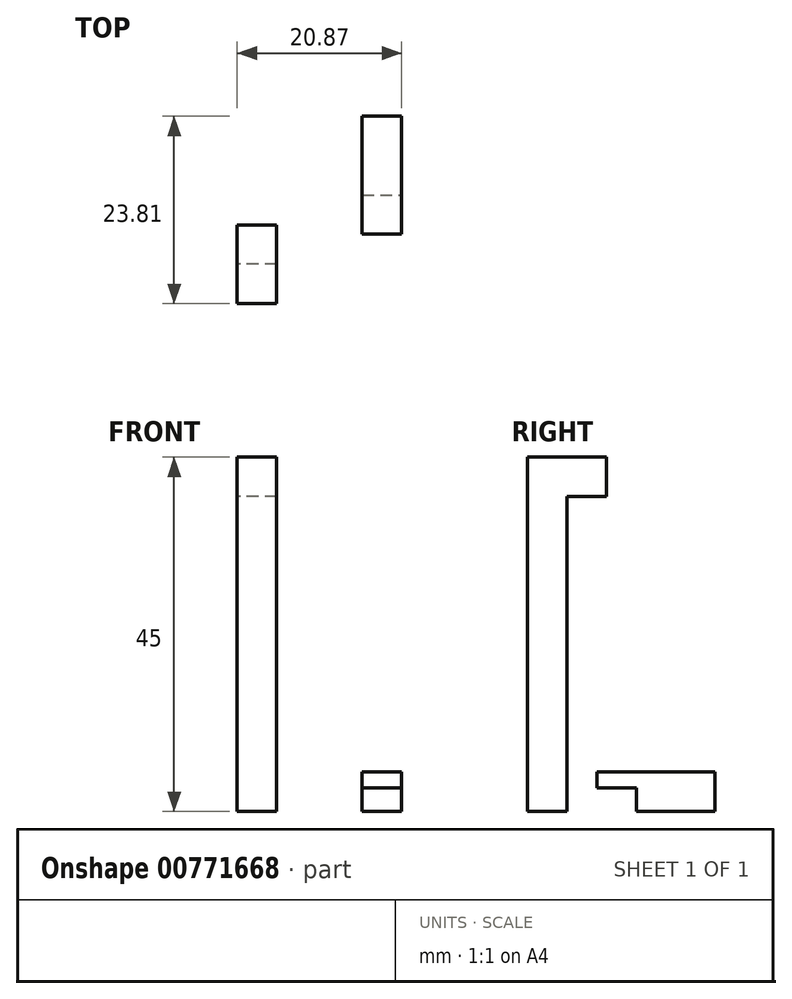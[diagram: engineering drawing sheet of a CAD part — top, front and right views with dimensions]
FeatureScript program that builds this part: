
annotation { "Feature Type Name" : "Feature", "Feature Type Description" : "" }
export const myFeature = defineFeature(function(context is Context, id is Id, definition is map)
    precondition{}
    {
        {
            var Q0;
            Q0=qCreatedBy(makeId("Top.planeOp"),FACE);
            var sketch = newSketch(context, id + "F0", { "sketchPlane" : qUnion([Q0])});
            skLineSegment(sketch, "E0.bottom", {"start": v(-55.01, -46.56) * mm, "end": v(-50.01, -46.56) * mm});
            skLineSegment(sketch, "E0.top", {"start": v(-55.01, -51.56) * mm, "end": v(-50.01, -51.56) * mm});
            skLineSegment(sketch, "E0.left", {"start": v(-55.01, -46.56) * mm, "end": v(-55.01, -51.56) * mm});
            skLineSegment(sketch, "E0.right", {"start": v(-50.01, -46.56) * mm, "end": v(-50.01, -51.56) * mm});
            skSolve(sketch);
        }
        {
            var Q0;
            Q0 = qSketchRegion(id + "F0", true);
            extrude(context, id + "F1", {"entities" : qUnion([Q0]), "depth" : 40 * mm, "offsetDistance" : 25 * mm});
        }
        {
            var Q0;
            Q0=makeQuery(id+"F1.opExtrude","CAP_FACE",FACE,{"disambiguationData":[OSD([sQuery(id+"F0.wireOp",EDGE,"E0.bottom"),sQuery(id+"F0.wireOp",EDGE,"E0.top"),sQuery(id+"F0.wireOp",EDGE,"E0.left"),sQuery(id+"F0.wireOp",EDGE,"E0.right")])],"isStart":false});
            var sketch = newSketch(context, id + "F2", { "sketchPlane" : qUnion([Q0])});
            skLineSegment(sketch, "E1.bottom", {"start": v(-55.01, -51.56) * mm, "end": v(-50.01, -51.56) * mm});
            skLineSegment(sketch, "E1.top", {"start": v(-55.01, -46.56) * mm, "end": v(-50.01, -46.56) * mm});
            skLineSegment(sketch, "E1.left", {"start": v(-55.01, -51.56) * mm, "end": v(-55.01, -46.56) * mm});
            skLineSegment(sketch, "E1.right", {"start": v(-50.01, -51.56) * mm, "end": v(-50.01, -46.56) * mm});
            skSolve(sketch);
        }
        {
            var Q0;
            Q0=makeQuery(id+"F2.imprint","IMPRINT",FACE,{"disambiguationData":[TD([[makeQuery(id+"F2.imprint","IMPRINT",EDGE,{"derivedFrom":sQuery(id+"F2.wireOp",EDGE,"E1.bottom")}),1.0]])]});
            var Q1;
            Q1 = qSketchRegion(id + "F2", true);
            extrude(context, id + "F3", {"entities" : qUnion([Q0, Q1]), "operationType" : NewBodyOperationType.ADD, "depth" : 5 * mm, "offsetDistance" : 25 * mm});
        }
        {
            var Q0;
            Q0=makeQuery(id+"F3.boolean.opBoolean","MERGE",FACE,{"derivedFrom":[makeQuery(id+"F1.opExtrude","SWEPT_FACE",FACE,{"disambiguationData":[OSD([sQuery(id+"F0.wireOp",EDGE,"E0.bottom")])]}),makeQuery(id+"F3.opExtrude","SWEPT_FACE",FACE,{"disambiguationData":[OSD([sQuery(id+"F2.wireOp",EDGE,"E1.top")])]})]});
            var sketch = newSketch(context, id + "F4", { "sketchPlane" : qUnion([Q0])});
            skLineSegment(sketch, "E2.bottom", {"start": v(50.01, 45) * mm, "end": v(55.01, 45) * mm});
            skLineSegment(sketch, "E2.top", {"start": v(50.01, 40) * mm, "end": v(55.01, 40) * mm});
            skLineSegment(sketch, "E2.left", {"start": v(50.01, 45) * mm, "end": v(50.01, 40) * mm});
            skLineSegment(sketch, "E2.right", {"start": v(55.01, 45) * mm, "end": v(55.01, 40) * mm});
            skSolve(sketch);
        }
        {
            var Q0;
            Q0 = qSketchRegion(id + "F4", true);
            extrude(context, id + "F5", {"entities" : qUnion([Q0]), "operationType" : NewBodyOperationType.ADD, "depth" : 5 * mm, "offsetDistance" : 25 * mm});
        }
        {
            var Q0;
            Q0=qCreatedBy(makeId("Top.planeOp"),FACE);
            var sketch = newSketch(context, id + "F6", { "sketchPlane" : qUnion([Q0])});
            skLineSegment(sketch, "E3.bottom", {"start": v(-39.14, -37.75) * mm, "end": v(-34.14, -37.75) * mm});
            skLineSegment(sketch, "E3.top", {"start": v(-39.14, -27.75) * mm, "end": v(-34.14, -27.75) * mm});
            skLineSegment(sketch, "E3.left", {"start": v(-39.14, -37.75) * mm, "end": v(-39.14, -27.75) * mm});
            skLineSegment(sketch, "E3.right", {"start": v(-34.14, -37.75) * mm, "end": v(-34.14, -27.75) * mm});
            skSolve(sketch);
        }
        {
            var Q0;
            Q0=makeQuery(id+"F6.imprint","IMPRINT",FACE,{"disambiguationData":[TD([[makeQuery(id+"F6.imprint","IMPRINT",EDGE,{"derivedFrom":sQuery(id+"F6.wireOp",EDGE,"E3.bottom")}),1.0]])]});
            extrude(context, id + "F7", {"entities" : qUnion([Q0]), "depth" : 5 * mm, "offsetDistance" : 25 * mm});
        }
        {
            var Q0;
            Q0=makeQuery(id+"F7.opExtrude","SWEPT_FACE",FACE,{"disambiguationData":[OSD([sQuery(id+"F6.wireOp",EDGE,"E3.bottom")])]});
            var sketch = newSketch(context, id + "F8", { "sketchPlane" : qUnion([Q0])});
            skLineSegment(sketch, "E4.bottom", {"start": v(-39.14, 5) * mm, "end": v(-34.14, 5) * mm});
            skLineSegment(sketch, "E4.top", {"start": v(-39.14, 3) * mm, "end": v(-34.14, 3) * mm});
            skLineSegment(sketch, "E4.left", {"start": v(-39.14, 5) * mm, "end": v(-39.14, 3) * mm});
            skLineSegment(sketch, "E4.right", {"start": v(-34.14, 5) * mm, "end": v(-34.14, 3) * mm});
            skSolve(sketch);
        }
        {
            var Q0;
            Q0 = qSketchRegion(id + "F8", true);
            extrude(context, id + "F9", {"entities" : qUnion([Q0]), "operationType" : NewBodyOperationType.ADD, "depth" : 5 * mm, "offsetDistance" : 25 * mm});
        }
    });
